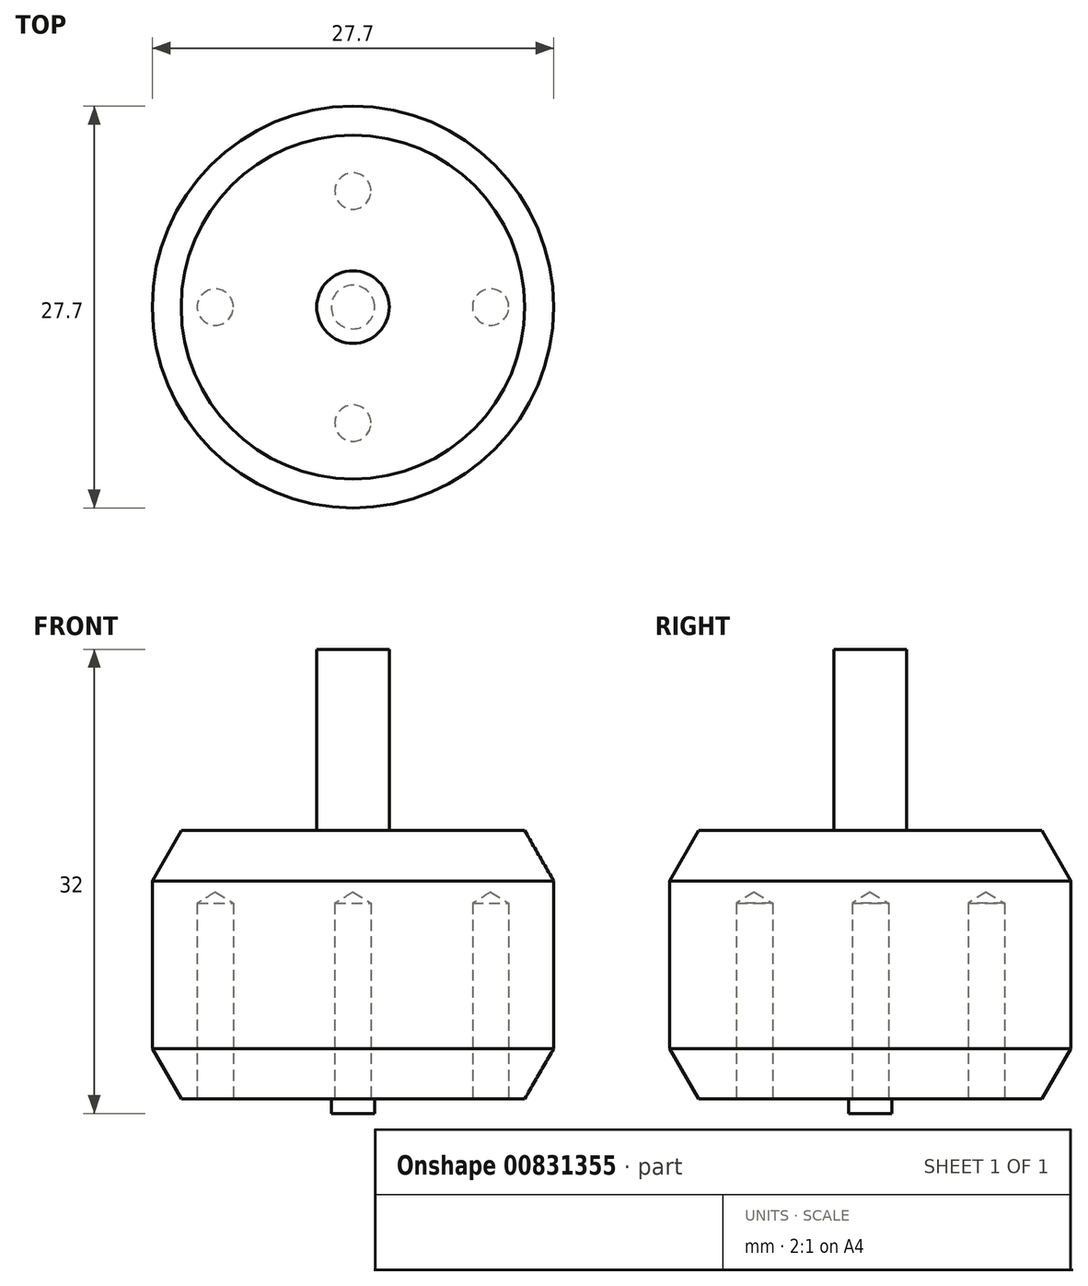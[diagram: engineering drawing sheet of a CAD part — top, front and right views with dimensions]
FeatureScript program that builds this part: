
annotation { "Feature Type Name" : "Feature", "Feature Type Description" : "" }
export const myFeature = defineFeature(function(context is Context, id is Id, definition is map)
    precondition{}
    {
        {
            var Q0;
            Q0=qCreatedBy(makeId("Top.planeOp"),FACE);
            var sketch = newSketch(context, id + "F0", { "sketchPlane" : qUnion([Q0])});
            skCircle(sketch, "E0", {"center": v(0, 0) * mm, "radius": 13.85 * mm});
            skSolve(sketch);
        }
        {
            var Q0;
            Q0 = qSketchRegion(id + "F0", true);
            extrude(context, id + "F1", {"entities" : qUnion([Q0]), "depth" : 18.5 * mm, "offsetDistance" : 25 * mm});
        }
        {
            var Q0;
            Q0=makeQuery(id+"F1.opExtrude","CAP_FACE",FACE,{"disambiguationData":[OSD([sQuery(id+"F0.wireOp",EDGE,"E0")])],"isStart":true});
            var sketch = newSketch(context, id + "F2", { "sketchPlane" : qUnion([Q0])});
            skCircle(sketch, "E1", {"center": v(0, 0) * mm, "radius": 1.5 * mm});
            skSolve(sketch);
        }
        {
            var Q0;
            Q0 = qSketchRegion(id + "F2", true);
            extrude(context, id + "F3", {"entities" : qUnion([Q0]), "operationType" : NewBodyOperationType.ADD, "depth" : 1 * mm, "offsetDistance" : 25 * mm});
        }
        {
            var Q0;
            Q0=makeQuery(id+"F1.opExtrude","CAP_FACE",FACE,{"disambiguationData":[OSD([sQuery(id+"F0.wireOp",EDGE,"E0")])],"isStart":false});
            var sketch = newSketch(context, id + "F4", { "sketchPlane" : qUnion([Q0])});
            skCircle(sketch, "E2", {"center": v(0, 0) * mm, "radius": 2.5 * mm});
            skSolve(sketch);
        }
        {
            var Q0;
            Q0 = qSketchRegion(id + "F4", true);
            extrude(context, id + "F5", {"entities" : qUnion([Q0]), "operationType" : NewBodyOperationType.ADD, "depth" : 12.5 * mm, "offsetDistance" : 25 * mm});
        }
        {
            var Q0;
            Q0=makeQuery(id+"F1.opExtrude","CAP_EDGE",EDGE,{"disambiguationData":[OSD([sQuery(id+"F0.wireOp",EDGE,"E0")])],"isStart":false});
            var Q1;
            Q1=makeQuery(id+"F1.opExtrude","CAP_EDGE",EDGE,{"disambiguationData":[OSD([sQuery(id+"F0.wireOp",EDGE,"E0")])],"isStart":true});
            chamfer(context, id + "F6", {"entities" : qUnion([Q0, Q1]), "chamferType" : ChamferType.OFFSET_ANGLE, "width" : 2 * mm, "oppositeDirection" : false, "angle" : 60 * degree, "tangentPropagation" : true});
        }
        {
            var Q0;
            Q0=makeQuery(id+"F1.opExtrude","CAP_FACE",FACE,{"disambiguationData":[OSD([sQuery(id+"F0.wireOp",EDGE,"E0")])],"isStart":true});
            var sketch = newSketch(context, id + "F7", { "sketchPlane" : qUnion([Q0])});
            skLineSegment(sketch, "E3", {"start": v(-9.5, 0) * mm, "end": v(9.5, 0) * mm, "construction": true});
            skLineSegment(sketch, "E4", {"start": v(0, -8) * mm, "end": v(0, 8) * mm, "construction": true});
            skSolve(sketch);
        }
        {
            var Q0;
            Q0=sQuery(id+"F7.wireOp",VERTEX,"E3.start");
            var Q1;
            Q1=sQuery(id+"F7.wireOp",VERTEX,"E4.end");
            var Q2;
            Q2=sQuery(id+"F7.wireOp",VERTEX,"E3.end");
            var Q3;
            Q3=sQuery(id+"F7.wireOp",VERTEX,"E4.start");
            var Q4;
            Q4=makeQuery(id+"F1.opExtrude","SWEPT_BODY",BODY,{"disambiguationData":[OSD([sQuery(id+"F0.wireOp",EDGE,"E0")])]});
            hole(context, id + "F8", {"style" : HoleStyle.SIMPLE, "endStyle" : HoleEndStyle.BLIND, "standardTappedOrClearance" : lookupTablePath({ "standard" : "ISO", "engagement" : "75%", "pitch" : "0.5 mm", "size" : "M3", "type" : "Tapped" }), "standardBlindInLast" : lookupTablePath({ "standard" : "ISO", "engagement" : "75%", "pitch" : "0.5 mm", "size" : "M3", "type" : "Tapped" }), "holeDiameter" : 2.5 * mm, "majorDiameter" : 3 * mm, "showTappedDepth" : true, "holeDepth" : 13.5 * mm, "isTappedThrough" : true, "tappedDepth" : 12 * mm, "tapClearance" : 3, "startFromSketch" : true, "locations" : qUnion([Q0, Q1, Q2, Q3]), "scope" : qUnion([Q4])});
        }
    });
